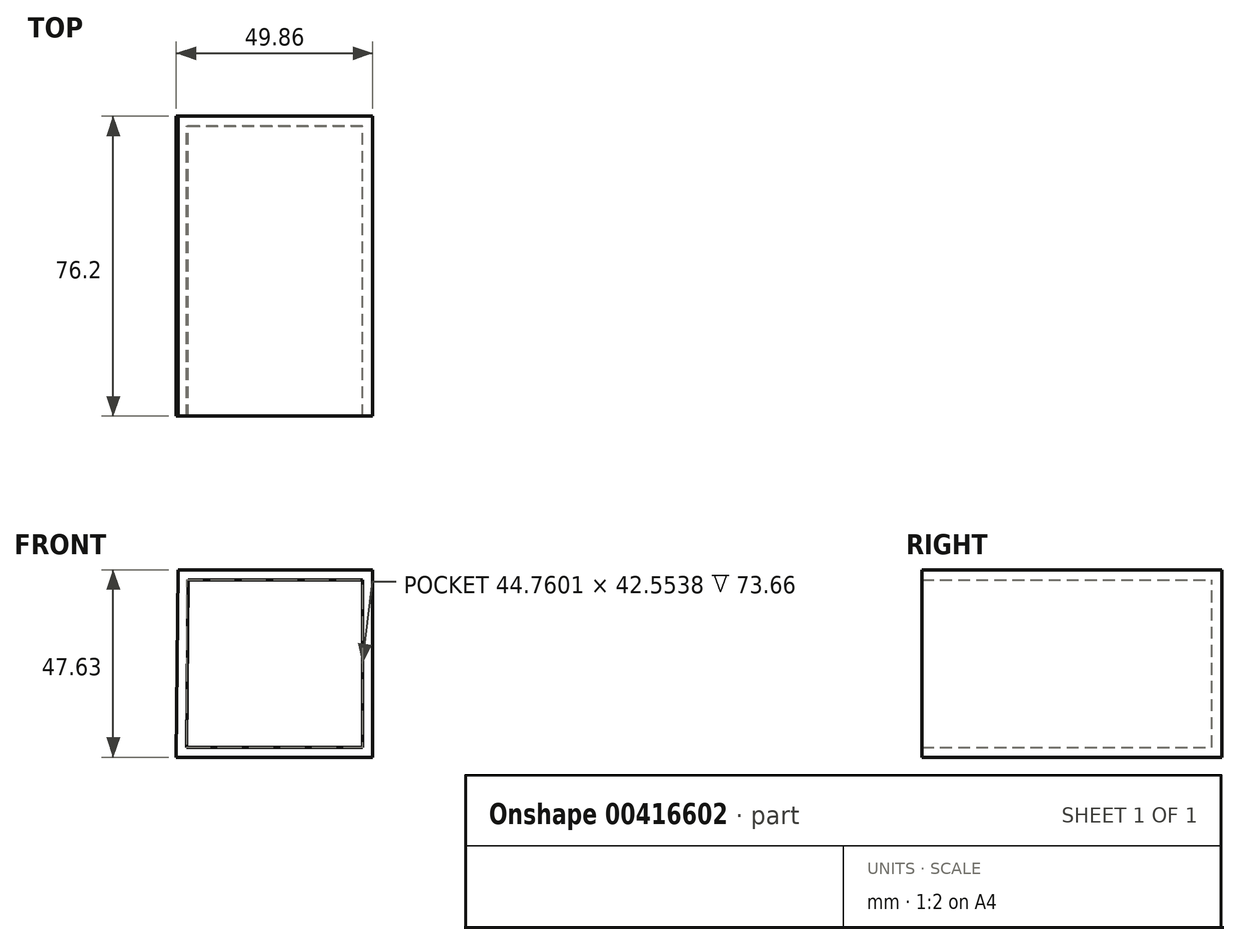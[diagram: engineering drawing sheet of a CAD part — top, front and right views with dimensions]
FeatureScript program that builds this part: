
annotation { "Feature Type Name" : "Feature", "Feature Type Description" : "" }
export const myFeature = defineFeature(function(context is Context, id is Id, definition is map)
    precondition{}
    {
        {
            var Q0;
            Q0=qCreatedBy(makeId("Front.planeOp"),FACE);
            var sketch = newSketch(context, id + "F0", { "sketchPlane" : qUnion([Q0])});
            skLineSegment(sketch, "E0", {"start": v(-21.09, 21.46) * mm, "end": v(28.28, 21.46) * mm});
            skLineSegment(sketch, "E1", {"start": v(28.28, -26.17) * mm, "end": v(-21.58, -26.17) * mm});
            skLineSegment(sketch, "E2", {"start": v(-21.58, -26.17) * mm, "end": v(-21.09, 21.46) * mm});
            skLineSegment(sketch, "E3", {"start": v(28.28, 21.46) * mm, "end": v(28.28, -26.17) * mm});
            skSolve(sketch);
        }
        {
            var Q0;
            Q0 = qSketchRegion(id + "F0", true);
            extrude(context, id + "F1", {"entities" : qUnion([Q0]), "depth" : 76.2 * mm});
        }
        {
            var Q0;
            Q0=makeQuery(id+"F1.opExtrude","CAP_FACE",FACE,{"disambiguationData":[OSD([sQuery(id+"F0.wireOp",EDGE,"E0"),sQuery(id+"F0.wireOp",EDGE,"E1"),sQuery(id+"F0.wireOp",EDGE,"E2"),sQuery(id+"F0.wireOp",EDGE,"E3")])],"isStart":false});
            shell(context, id + "F2", {"entities" : qUnion([Q0]), "thickness" : 2.54 * mm});
        }
    });
